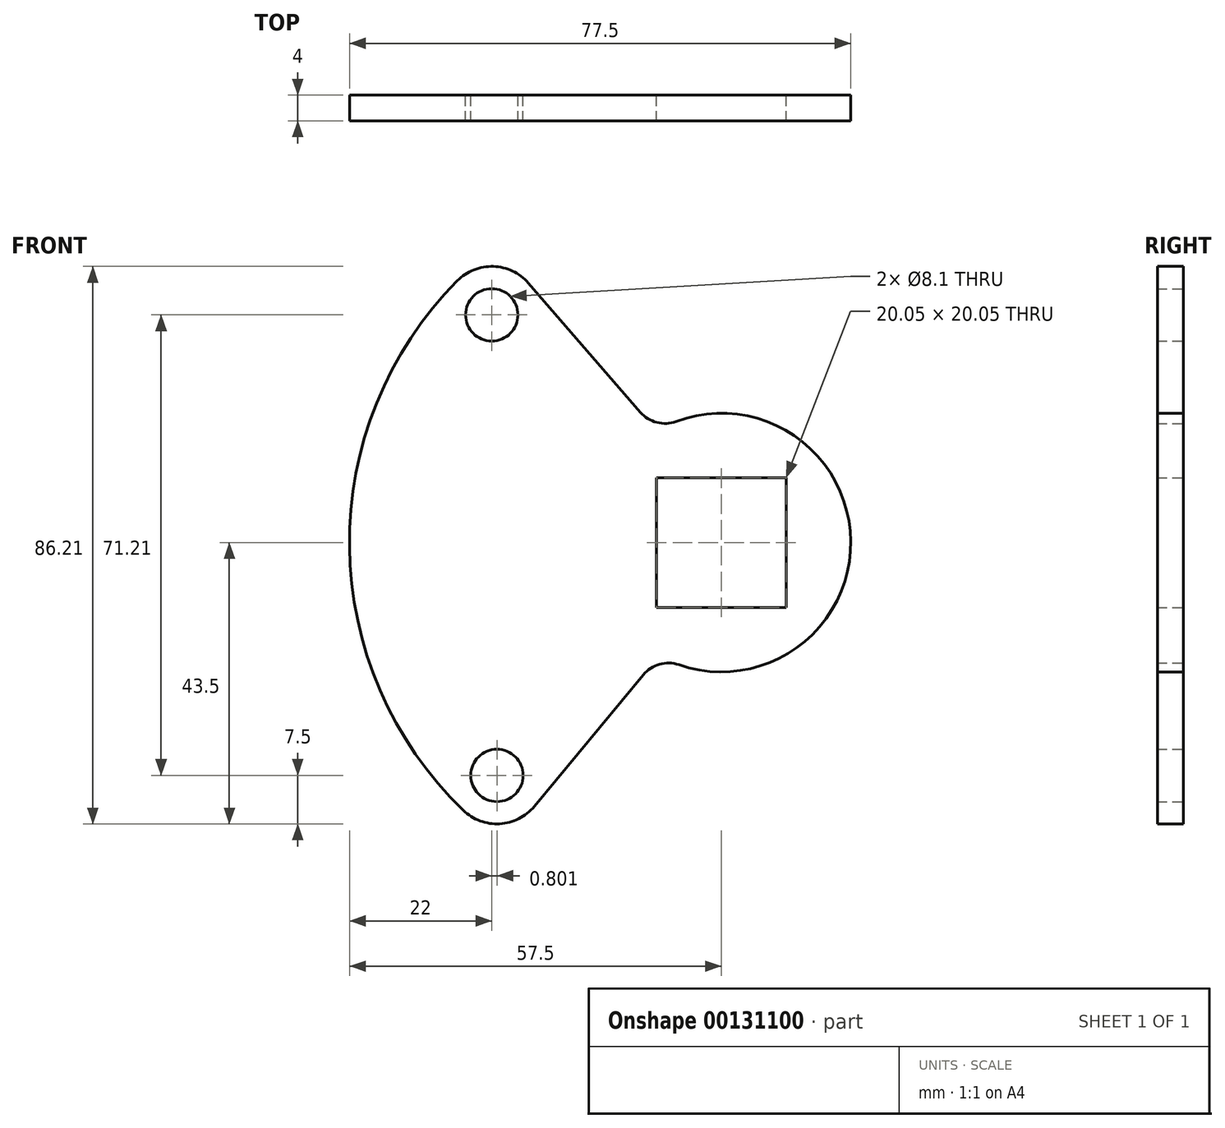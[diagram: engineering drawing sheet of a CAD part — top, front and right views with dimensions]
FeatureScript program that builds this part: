
annotation { "Feature Type Name" : "Feature", "Feature Type Description" : "" }
export const myFeature = defineFeature(function(context is Context, id is Id, definition is map)
    precondition{}
    {
        {
            var Q0;
            Q0=qCreatedBy(makeId("Front.planeOp"),FACE);
            var sketch = newSketch(context, id + "F0", { "sketchPlane" : qUnion([Q0])});
            skLineSegment(sketch, "E0.bottom", {"start": v(10.03, -10.03) * mm, "end": v(-10.03, -10.03) * mm});
            skLineSegment(sketch, "E0.top", {"start": v(10.03, 10.03) * mm, "end": v(-10.02, 10.02) * mm});
            skLineSegment(sketch, "E0.left", {"start": v(10.03, -10.02) * mm, "end": v(10.03, 10.02) * mm});
            skLineSegment(sketch, "E0.right", {"start": v(-10.03, -10.03) * mm, "end": v(-10.02, 10.02) * mm});
            skPoint(sketch, "E0.middle", {"position": v(0, 0) * mm});
            skCircle(sketch, "E1", {"center": v(0, 0) * mm, "radius": 20 * mm});
            skCircle(sketch, "E2", {"center": v(0, 0) * mm, "radius": 57.5 * mm});
            skCircle(sketch, "E3", {"center": v(0, 0) * mm, "radius": 50 * mm, "construction": true});
            skPoint(sketch, "E4", {"position": v(-35.5, 35.21) * mm});
            skPoint(sketch, "E5", {"position": v(-34.7, -36) * mm});
            skPoint(sketch, "E5.positionSnap0", {"position": v(-10.02, 0) * mm});
            skCircle(sketch, "E6", {"center": v(-34.7, -36) * mm, "radius": 7.5 * mm});
            skCircle(sketch, "E7", {"center": v(-35.5, 35.21) * mm, "radius": 7.5 * mm});
            skLineSegment(sketch, "E8", {"start": v(-29.83, 40.12) * mm, "end": v(-10.04, 17.3) * mm});
            skLineSegment(sketch, "E9", {"start": v(-28.92, -40.79) * mm, "end": v(-9.65, -17.52) * mm});
            skSolve(sketch);
        }
        {
            var Q0;
            Q0=makeQuery(id+"F0.imprint","IMPRINT",FACE,{"disambiguationData":[TD([[makeQuery(id+"F0.imprint","IMPRINT",EDGE,{"derivedFrom":sQuery(id+"F0.wireOp",EDGE,"E0.bottom")}),1.0]])]});
            var Q1;
            {var subQ0=sQuery(id+"F0.wireOp",EDGE,"E8");Q1=makeQuery(id+"F0.imprint","IMPRINT",FACE,{"disambiguationData":[TD([[makeQuery(id+"F0.imprint","IMPRINT",EDGE,{"derivedFrom":subQ0}),-1.0]])]});}
            var Q2;
            {var subQ0=sQuery(id+"F0.wireOp",EDGE,"E7");var subQ1=makeQuery(id+"F0.imprint","INTERSECT",VERTEX,{"derivedFrom":[subQ0,sQuery(id+"F0.wireOp",EDGE,"E8")]});Q2=makeQuery(id+"F0.imprint","IMPRINT",FACE,{"disambiguationData":[TD([[makeQuery(id+"F0.imprint","IMPRINT",EDGE,{"disambiguationData":[TD([[subQ1,-1.0]])],"derivedFrom":subQ0}),1.0]])]});}
            var Q3;
            {var subQ0=sQuery(id+"F0.wireOp",EDGE,"E6");var subQ1=makeQuery(id+"F0.imprint","INTERSECT",VERTEX,{"derivedFrom":[subQ0,sQuery(id+"F0.wireOp",EDGE,"E9")]});Q3=makeQuery(id+"F0.imprint","IMPRINT",FACE,{"disambiguationData":[TD([[makeQuery(id+"F0.imprint","IMPRINT",EDGE,{"disambiguationData":[TD([[subQ1,1.0]])],"derivedFrom":subQ0}),1.0]])]});}
            extrude(context, id + "F1", {"entities" : qUnion([Q0, Q1, Q2, Q3]), "depth" : 4 * mm});
        }
        {
            var Q0;
            Q0=sQuery(id+"F0.wireOp",VERTEX,"E5");
            var Q1;
            Q1=sQuery(id+"F0.wireOp",VERTEX,"E4");
            var Q2;
            Q2=makeQuery(id+"F1.opExtrude","SWEPT_BODY",BODY,{"disambiguationData":[OSD([sQuery(id+"F0.wireOp",EDGE,"E0.bottom"),sQuery(id+"F0.wireOp",EDGE,"E0.top"),sQuery(id+"F0.wireOp",EDGE,"E0.left"),sQuery(id+"F0.wireOp",EDGE,"E0.right"),sQuery(id+"F0.wireOp",EDGE,"E1"),sQuery(id+"F0.wireOp",EDGE,"E2"),sQuery(id+"F0.wireOp",EDGE,"f7iVyOiV-7fWC-Twld-DPCY-SPoEPPuV7R9u"),sQuery(id+"F0.wireOp",EDGE,"vaposIsL-FUod-5LYb-vS1i-a8I1H2uGAQ2Y")])]});
            hole(context, id + "F2", {"style" : HoleStyle.SIMPLE, "endStyle" : HoleEndStyle.THROUGH, "oppositeDirection" : true, "holeDiameter" : 8.1 * mm, "locations" : qUnion([Q0, Q1]), "scope" : qUnion([Q2]), "isTappedThrough" : true});
        }
        {
            var Q0;
            Q0=makeQuery(id+"F1.opExtrude","SWEPT_EDGE",EDGE,{"disambiguationData":[OSD([sQuery(id+"F0.wireOp",EDGE,"E1"),sQuery(id+"F0.wireOp",EDGE,"E8")])]});
            var Q1;
            Q1=makeQuery(id+"F1.opExtrude","SWEPT_EDGE",EDGE,{"disambiguationData":[OSD([sQuery(id+"F0.wireOp",EDGE,"E1"),sQuery(id+"F0.wireOp",EDGE,"E9")])]});
            fillet(context, id + "F3", {"entities" : qUnion([Q0, Q1]), "radius" : 5 * mm, "tangentPropagation" : true, "allowEdgeOverflow" : false});
        }
    });
